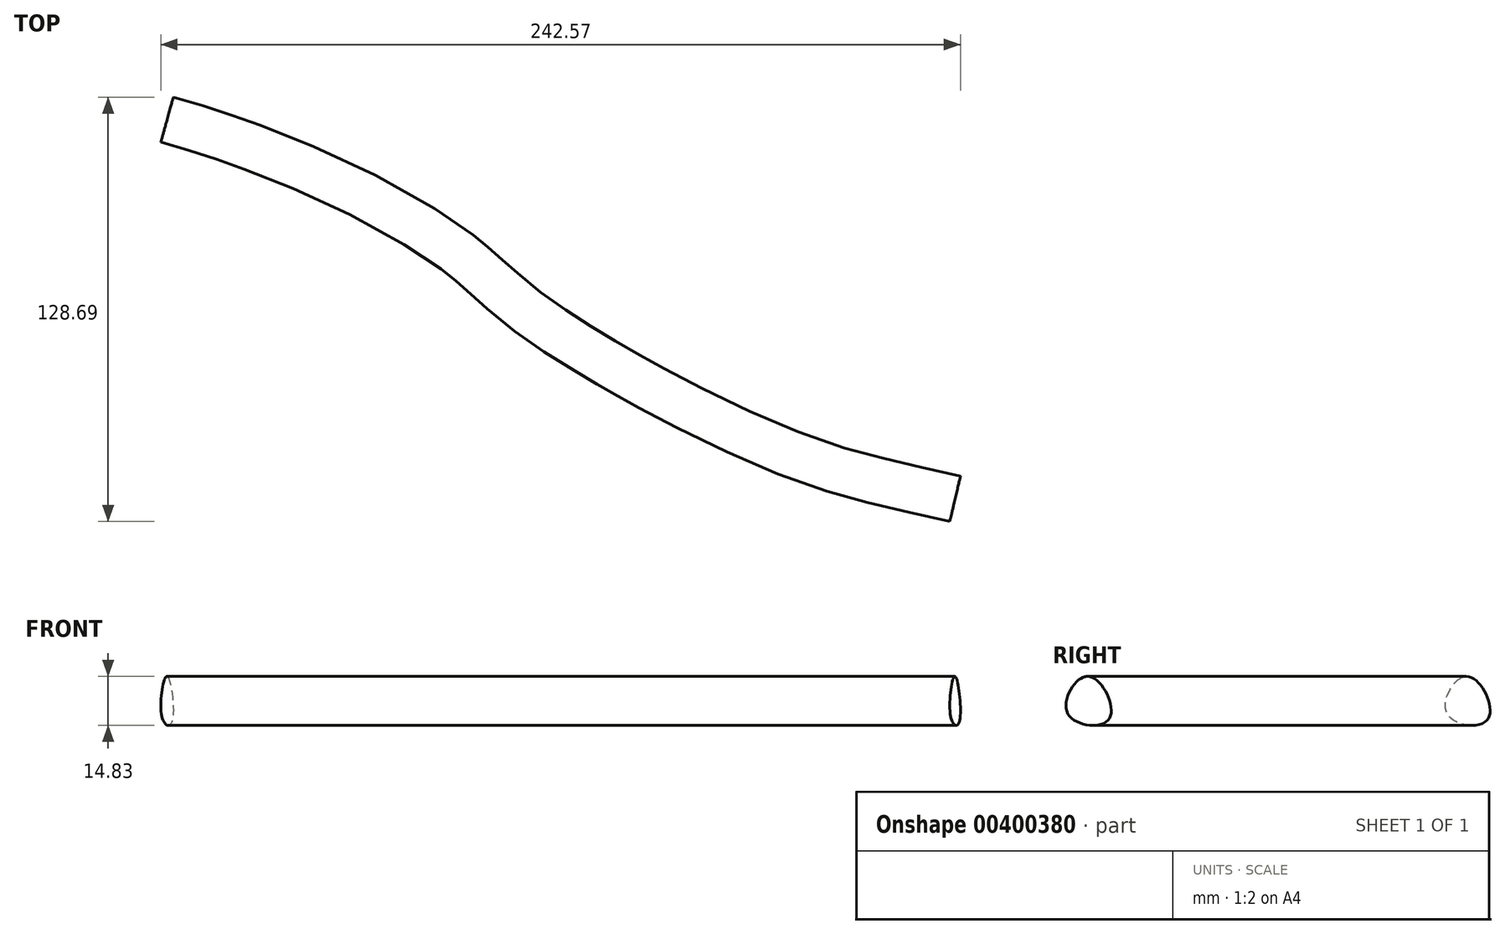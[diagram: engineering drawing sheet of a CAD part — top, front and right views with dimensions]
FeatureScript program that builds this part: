
annotation { "Feature Type Name" : "Feature", "Feature Type Description" : "" }
export const myFeature = defineFeature(function(context is Context, id is Id, definition is map)
    precondition{}
    {
        {
            var Q0;
            Q0=qCreatedBy(makeId("Top.planeOp"),FACE);
            var sketch = newSketch(context, id + "F0", { "sketchPlane" : qUnion([Q0])});
            skFitSpline(sketch, "E0", {"points": [v(-117.12, 78.31) * mm, v(-31.38, 39.7) * mm, v(-7.47, 19.66) * mm, v(70, -22.33) * mm, v(122.01, -36.72) * mm], "startDerivative": vector(366.37, -102.02) * mm, "endDerivative": vector(259.74, -61.55) * mm});
            skSolve(sketch);
        }
        {
            var Q0;
            Q0=sQuery(id+"F0.wireOp",EDGE,"E0");
            var Q1;
            Q1=sQuery(id+"F0.wireOp",VERTEX,"E0.4.internal");
            cPlane(context, id + "F1", {"entities" : qUnion([Q0, Q1]), "cplaneType" : CPlaneType.CURVE_POINT, "offset" : 25.4 * mm, "width" : 152.4 * mm, "height" : 152.4 * mm});
        }
        {
            var Q0;
            Q0=qCreatedBy(id+"F1.planeOp",FACE);
            var sketch = newSketch(context, id + "F2", { "sketchPlane" : qUnion([Q0])});
            skFitSpline(sketch, "E1", {"points": [v(-7.15, 4.75) * mm, v(0, 0) * mm, v(0, -8.82) * mm, v(-12.04, -6.24) * mm, v(-7.15, 4.75) * mm]});
            skSolve(sketch);
        }
        {
            var Q0;
            Q0=makeQuery(id+"F2.imprint","IMPRINT",FACE,{"disambiguationData":[TD([[makeQuery(id+"F2.imprint","IMPRINT",EDGE,{"derivedFrom":sQuery(id+"F2.wireOp",EDGE,"E1")}),-1.0]])]});
            var Q1;
            Q1=sQuery(id+"F0.wireOp",EDGE,"E0");
            sweep(context, id + "F3", {"profiles" : qUnion([Q0]), "path" : qUnion([Q1])});
        }
    });
